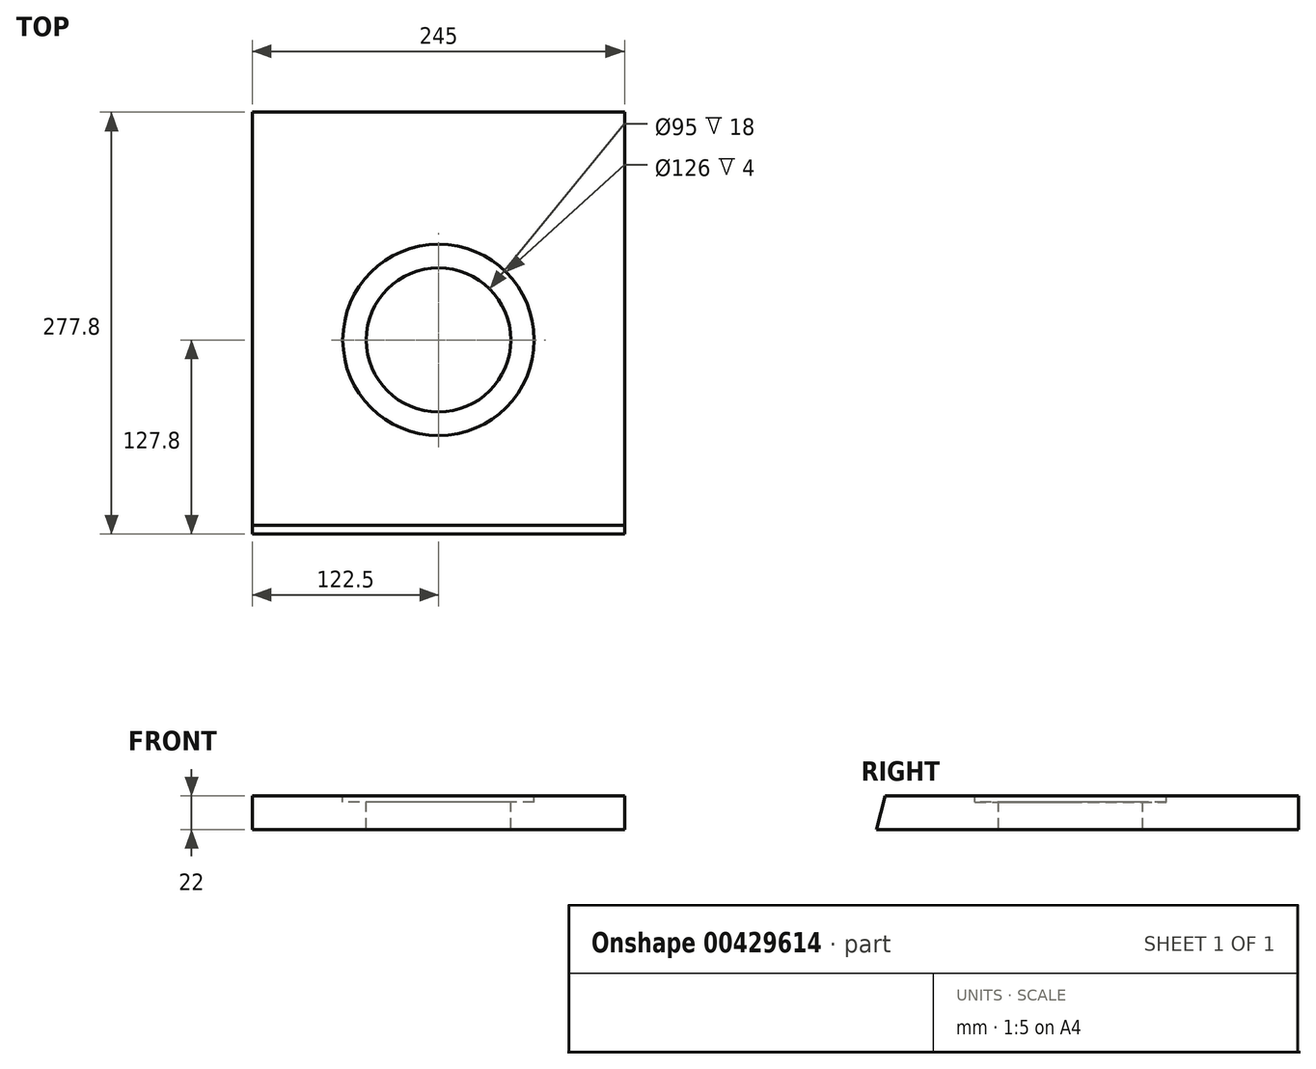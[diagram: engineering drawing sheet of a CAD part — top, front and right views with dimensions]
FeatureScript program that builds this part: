
annotation { "Feature Type Name" : "Feature", "Feature Type Description" : "" }
export const myFeature = defineFeature(function(context is Context, id is Id, definition is map)
    precondition{}
    {
        {
            var Q0;
            Q0=qCreatedBy(makeId("Top.planeOp"),FACE);
            var sketch = newSketch(context, id + "F0", { "sketchPlane" : qUnion([Q0])});
            skLineSegment(sketch, "E0.bottom", {"start": v(-122.5, 138.9) * mm, "end": v(122.5, 138.9) * mm});
            skLineSegment(sketch, "E0.top", {"start": v(-122.5, -138.9) * mm, "end": v(122.5, -138.9) * mm});
            skLineSegment(sketch, "E0.left", {"start": v(-122.5, 138.9) * mm, "end": v(-122.5, -138.9) * mm});
            skLineSegment(sketch, "E0.right", {"start": v(122.5, 138.9) * mm, "end": v(122.5, -138.9) * mm});
            skPoint(sketch, "E0.middle", {"position": v(0, 0) * mm});
            skSolve(sketch);
        }
        {
            var Q0;
            Q0 = qSketchRegion(id + "F0", true);
            extrude(context, id + "F1", {"entities" : qUnion([Q0]), "depth" : 22 * mm});
        }
        {
            var Q0;
            Q0=makeQuery(id+"F1.opExtrude","CAP_FACE",FACE,{"disambiguationData":[OSD([sQuery(id+"F0.wireOp",EDGE,"E0.bottom"),sQuery(id+"F0.wireOp",EDGE,"E0.top"),sQuery(id+"F0.wireOp",EDGE,"E0.left"),sQuery(id+"F0.wireOp",EDGE,"E0.right")])],"isStart":false});
            var sketch = newSketch(context, id + "F2", { "sketchPlane" : qUnion([Q0])});
            skLineSegment(sketch, "E1", {"start": v(0, -138.9) * mm, "end": v(0, 138.9) * mm, "construction": true});
            skPoint(sketch, "E2", {"position": v(0, -11.1) * mm});
            skSolve(sketch);
        }
        {
            var Q0;
            Q0=sQuery(id+"F2.wireOp",VERTEX,"E2");
            var Q1;
            Q1=makeQuery(id+"F1.opExtrude","SWEPT_BODY",BODY,{"disambiguationData":[OSD([sQuery(id+"F0.wireOp",EDGE,"E0.bottom"),sQuery(id+"F0.wireOp",EDGE,"E0.top"),sQuery(id+"F0.wireOp",EDGE,"E0.left"),sQuery(id+"F0.wireOp",EDGE,"E0.right")])]});
            hole(context, id + "F3", {"style" : HoleStyle.SIMPLE, "endStyle" : HoleEndStyle.THROUGH, "holeDiameter" : 95 * mm, "isTappedThrough" : true, "tappedDepth" : 12 * mm, "tapClearance" : 3, "locations" : qUnion([Q0]), "scope" : qUnion([Q1])});
        }
        {
            var Q0;
            Q0=makeQuery(id+"F1.opExtrude","CAP_FACE",FACE,{"disambiguationData":[OSD([sQuery(id+"F0.wireOp",EDGE,"E0.bottom"),sQuery(id+"F0.wireOp",EDGE,"E0.top"),sQuery(id+"F0.wireOp",EDGE,"E0.left"),sQuery(id+"F0.wireOp",EDGE,"E0.right")])],"isStart":false});
            var sketch = newSketch(context, id + "F4", { "sketchPlane" : qUnion([Q0])});
            skCircle(sketch, "E3", {"center": v(0, -11.1) * mm, "radius": 63 * mm});
            skSolve(sketch);
        }
        {
            var Q0;
            Q0 = qSketchRegion(id + "F4", true);
            extrude(context, id + "F5", {"entities" : qUnion([Q0]), "operationType" : NewBodyOperationType.REMOVE, "oppositeDirection" : true, "depth" : 4 * mm});
        }
        {
            var Q0;
            Q0=makeQuery(id+"F1.opExtrude","SWEPT_FACE",FACE,{"disambiguationData":[OSD([sQuery(id+"F0.wireOp",EDGE,"E0.left")])]});
            var sketch = newSketch(context, id + "F6", { "sketchPlane" : qUnion([Q0])});
            skLineSegment(sketch, "E4", {"start": v(138.9, 0) * mm, "end": v(133, 22) * mm});
            skLineSegment(sketch, "E5", {"start": v(133, 22) * mm, "end": v(138.9, 22) * mm});
            skLineSegment(sketch, "E6", {"start": v(138.9, 22) * mm, "end": v(138.9, 0) * mm});
            skSolve(sketch);
        }
        {
            var Q0;
            Q0 = qSketchRegion(id + "F6", true);
            extrude(context, id + "F7", {"entities" : qUnion([Q0]), "operationType" : NewBodyOperationType.REMOVE, "endBound" : BoundingType.THROUGH_ALL, "oppositeDirection" : true, "depth" : 25 * mm});
        }
    });
